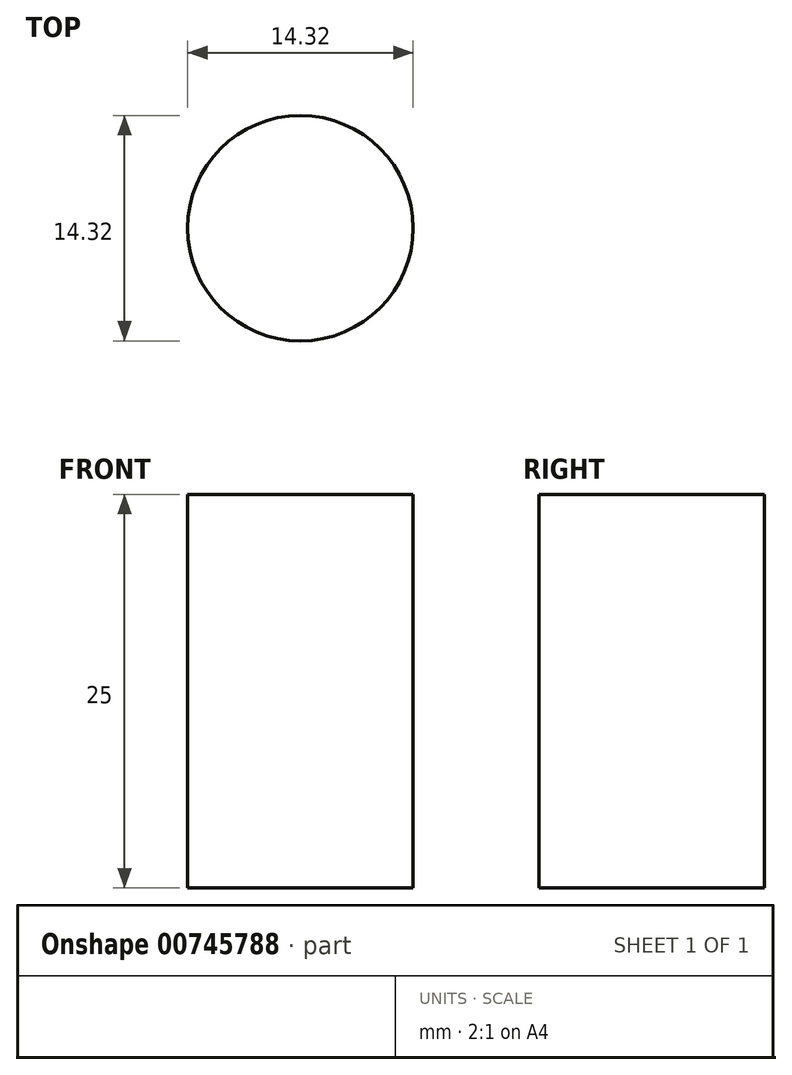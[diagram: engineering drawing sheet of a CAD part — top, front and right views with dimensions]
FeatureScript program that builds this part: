
annotation { "Feature Type Name" : "Feature", "Feature Type Description" : "" }
export const myFeature = defineFeature(function(context is Context, id is Id, definition is map)
    precondition{}
    {
        {
            var Q0;
            Q0=qCreatedBy(makeId("Top.planeOp"),FACE);
            var sketch = newSketch(context, id + "F0", { "sketchPlane" : qUnion([Q0])});
            skLineSegment(sketch, "E0.bottom", {"start": v(-50.18, 52.36) * mm, "end": v(50.18, 52.36) * mm});
            skLineSegment(sketch, "E0.top", {"start": v(-50.18, -52.36) * mm, "end": v(50.18, -52.36) * mm});
            skLineSegment(sketch, "E0.left", {"start": v(-50.18, 52.36) * mm, "end": v(-50.18, -52.36) * mm});
            skLineSegment(sketch, "E0.right", {"start": v(50.18, 52.36) * mm, "end": v(50.18, -52.36) * mm});
            skPoint(sketch, "E0.middle", {"position": v(0, 0) * mm});
            skCircle(sketch, "E1", {"center": v(-28.3, 36.23) * mm, "radius": 7.16 * mm});
            skCircle(sketch, "E2", {"center": v(29.4, 36.23) * mm, "radius": 6.2 * mm});
            skCircle(sketch, "E3", {"center": v(29.67, -36.78) * mm, "radius": 7.27 * mm});
            skSolve(sketch);
        }
        {
            var Q0;
            Q0=makeQuery(id+"F0.imprint","IMPRINT",FACE,{"disambiguationData":[TD([[makeQuery(id+"F0.imprint","IMPRINT",EDGE,{"derivedFrom":sQuery(id+"F0.wireOp",EDGE,"E1")}),1.0]])]});
            extrude(context, id + "F1", {"entities" : qUnion([Q0]), "depth" : 25 * mm, "offsetDistance" : 25 * mm});
        }
    });
